# Revit family: PRE030041
name_source: partatom
category: Appareils sanitaires
revit_build: Autodesk Revit 2017 (Build: 20160225_1515(x64)
units: mm (PartAtom-declared; Revit-internal decimal feet)

## family parameters
Basée sur le plan de construction = Oui
Cote de connecteur circulaire = Utiliser le diamètre
Couper avec des vides une fois chargée = Non
Partagée = Non
Point de calcul de pièce = Non
Toujours verticalement = Oui
Type d'élément = Normal

## types (3) — shared parameters
1 = Oui
Adresse = 7 RUE RACINE  92542 MONTROUGE CEDEX FRANCE
Diamètre nominal = 15 mm  [stored 0.0492126 ft]
Elévation par défaut = 1219 mm
Fabricant = LES ROBINETS PRESTO SA
Flux = 0.1 L/s
Material = PRESTO Chrome
Perte de charge = 0.0 Pa
URL Fabricant = http://www.prestodatashare.com
Variantes = 75638 -75639 -75640
zero-valued in all types: Hauteur, Largeur, Profondeur

## per-type parameters (varying)
| type | 2 | 3 | 4 | 5 | Polantis code | Reference |
| 75638 Presto Mastermix mitigeur thermostatique de douche | Oui | Non | Oui | Non | PRE030041 | 75638 |
| 75639 Presto Mastermix mitigeur thermostatique de douche | Non | Oui | Non | Oui | PRE030041a | 75639 |
| 75640 Presto Mastermix mitigeur thermostatique de douche | Oui | Oui | Non | Non | PRE030041b | 75640 |

note: column(s) folded — value = type name in every type: Modèle

note: [stored X ft] marks values corroborated as IEEE doubles in the binary element streams (Revit-internal decimal feet)

## geometry (parser evidence)
native form markers: Sweep x1
no freeform markers — native parametric forms only
